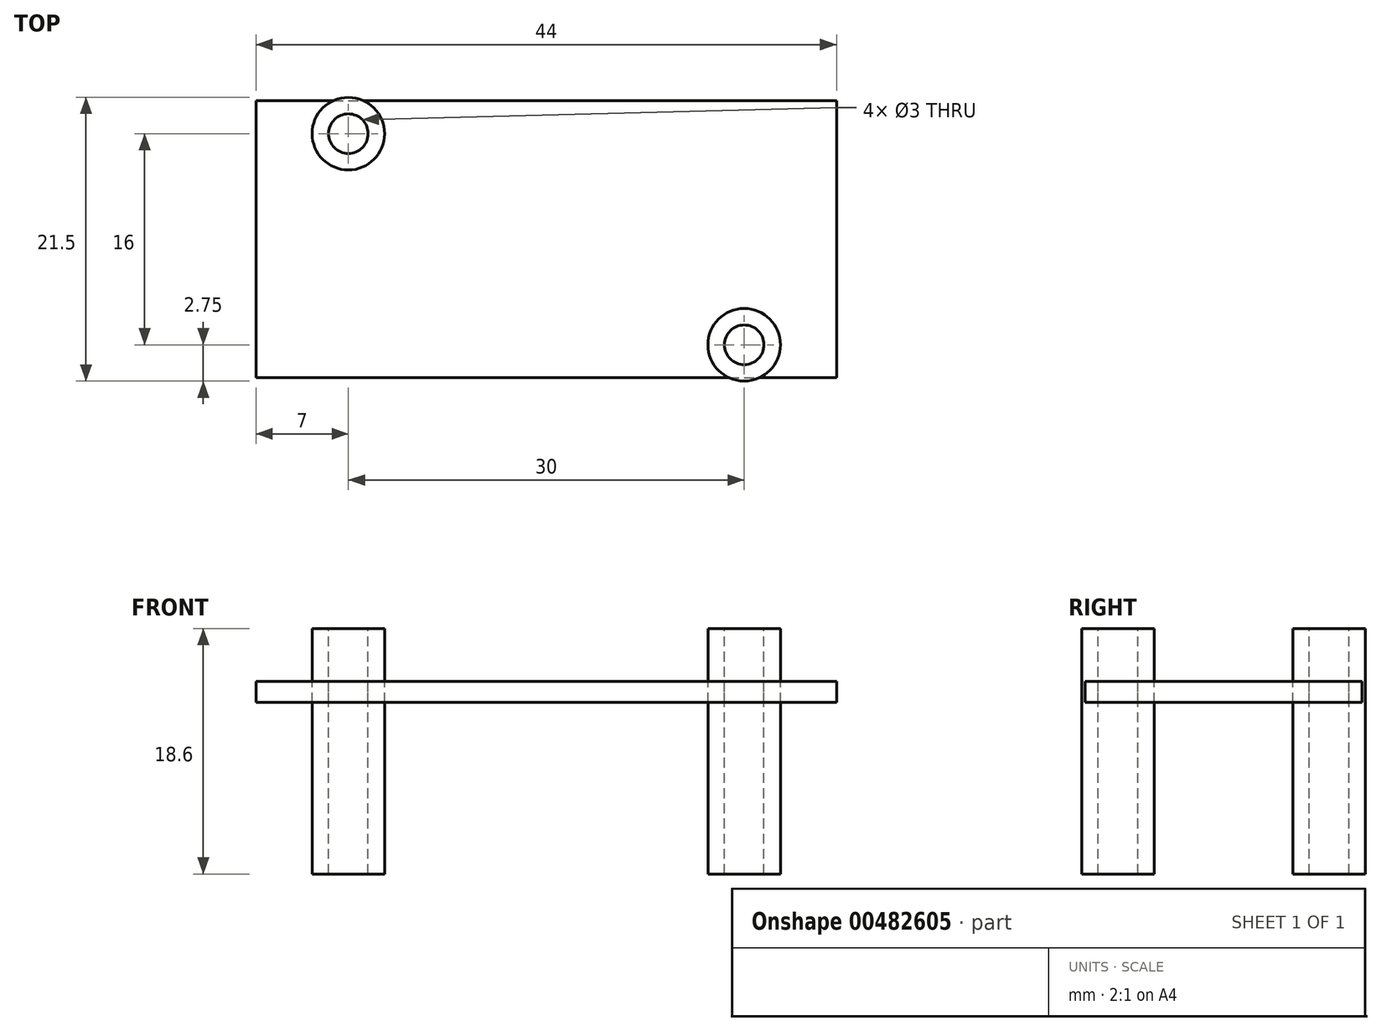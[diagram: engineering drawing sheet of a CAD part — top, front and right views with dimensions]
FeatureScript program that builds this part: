
annotation { "Feature Type Name" : "Feature", "Feature Type Description" : "" }
export const myFeature = defineFeature(function(context is Context, id is Id, definition is map)
    precondition{}
    {
        {
            var Q0;
            Q0=qCreatedBy(makeId("Top.planeOp"),FACE);
            var sketch = newSketch(context, id + "F0", { "sketchPlane" : qUnion([Q0])});
            skLineSegment(sketch, "E0.bottom", {"start": v(-22, 10.5) * mm, "end": v(22, 10.5) * mm});
            skLineSegment(sketch, "E0.top", {"start": v(-22, -10.5) * mm, "end": v(22, -10.5) * mm});
            skLineSegment(sketch, "E0.left", {"start": v(-22, 10.5) * mm, "end": v(-22, -10.5) * mm});
            skLineSegment(sketch, "E0.right", {"start": v(22, 10.5) * mm, "end": v(22, -10.5) * mm});
            skPoint(sketch, "E0.middle", {"position": v(0, 0) * mm});
            skCircle(sketch, "E1", {"center": v(-15, 8) * mm, "radius": 1.5 * mm});
            skCircle(sketch, "E2", {"center": v(15, -8) * mm, "radius": 1.5 * mm});
            skSolve(sketch);
        }
        {
            var Q0;
            Q0 = qSketchRegion(id + "F0", true);
            extrude(context, id + "F1", {"entities" : qUnion([Q0]), "oppositeDirection" : true, "depth" : 1.6 * mm, "offsetDistance" : 25 * mm});
        }
        {
            var Q0;
            Q0=makeQuery(id+"F1.opExtrude","CAP_FACE",FACE,{"disambiguationData":[OSD([sQuery(id+"F0.wireOp",EDGE,"E0.bottom"),sQuery(id+"F0.wireOp",EDGE,"E0.top"),sQuery(id+"F0.wireOp",EDGE,"E0.left"),sQuery(id+"F0.wireOp",EDGE,"E0.right"),sQuery(id+"F0.wireOp",EDGE,"E1"),sQuery(id+"F0.wireOp",EDGE,"E2")])],"isStart":false});
            var sketch = newSketch(context, id + "F2", { "sketchPlane" : qUnion([Q0])});
            skCircle(sketch, "E3.0", {"center": v(-15, -8) * mm, "radius": 1.5 * mm});
            skCircle(sketch, "E4.0", {"center": v(15, 8) * mm, "radius": 1.5 * mm});
            skCircle(sketch, "E5.0", {"center": v(-15, -8) * mm, "radius": 2.75 * mm});
            skCircle(sketch, "E6.0", {"center": v(15, 8) * mm, "radius": 2.75 * mm});
            skSolve(sketch);
        }
        {
            var Q0;
            Q0 = qSketchRegion(id + "F2", true);
            extrude(context, id + "F3", {"entities" : qUnion([Q0]), "depth" : 13 * mm, "offsetDistance" : 25 * mm, "hasSecondDirection" : true, "secondDirectionOppositeDirection" : true, "secondDirectionDepth" : (1.6 + 4) * mm});
        }
    });
